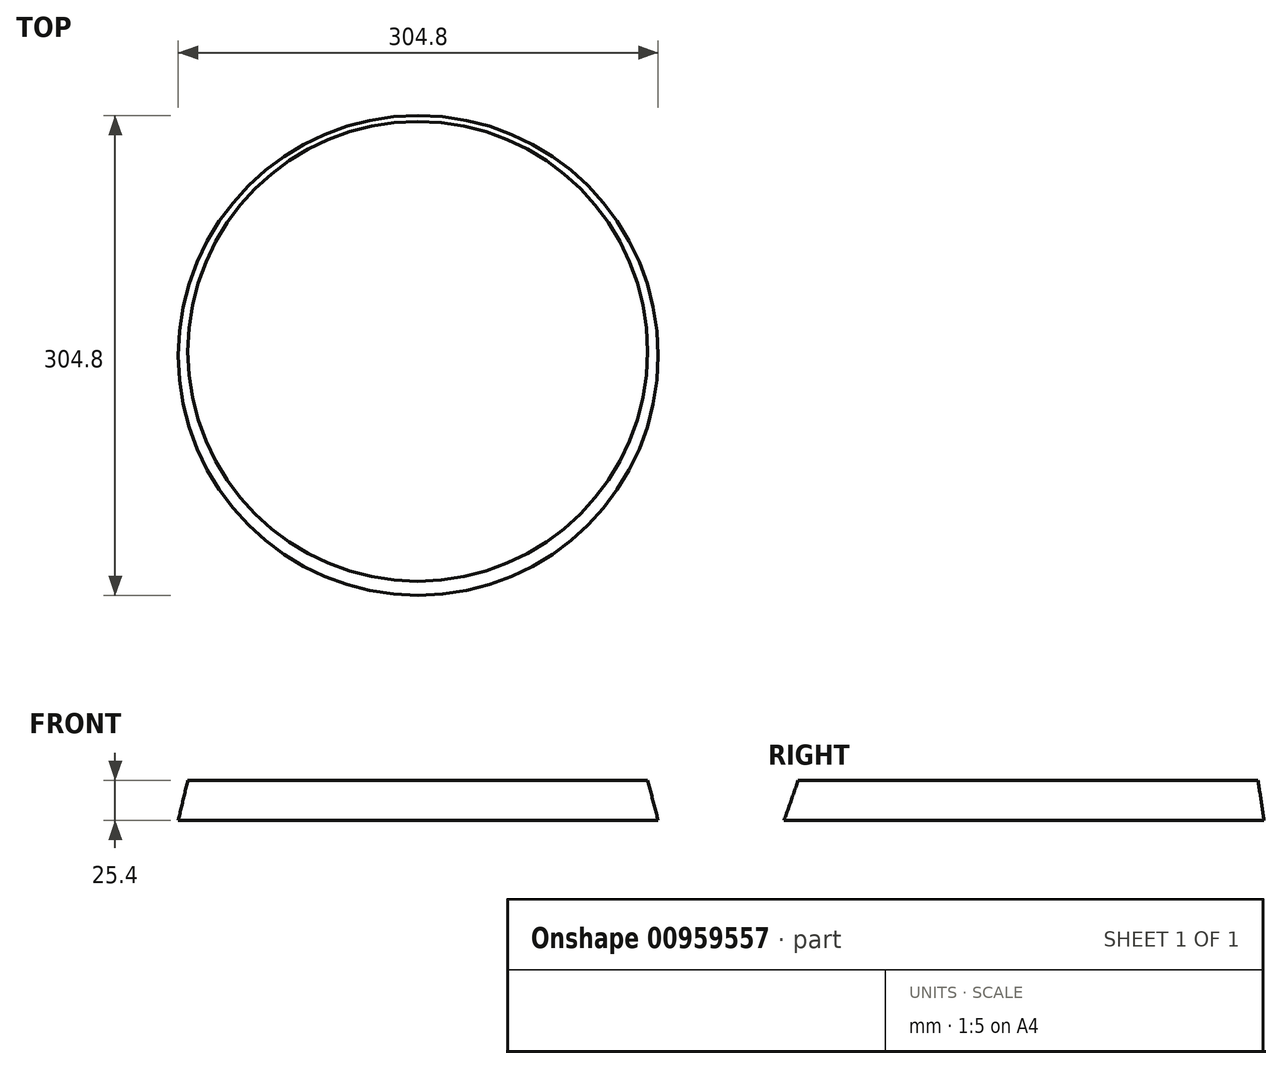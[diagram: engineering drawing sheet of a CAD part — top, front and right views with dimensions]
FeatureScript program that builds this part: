
annotation { "Feature Type Name" : "Feature", "Feature Type Description" : "" }
export const myFeature = defineFeature(function(context is Context, id is Id, definition is map)
    precondition{}
    {
        {
            var Q0;
            Q0=qCreatedBy(makeId("Top.planeOp"),FACE);
            var sketch = newSketch(context, id + "F0", { "sketchPlane" : qUnion([Q0])});
            skCircle(sketch, "E0", {"center": v(-35.68, 43.57) * mm, "radius": 152.4 * mm});
            skSolve(sketch);
        }
        {
            var Q0;
            Q0=qCreatedBy(makeId("Top.planeOp"),FACE);
            cPlane(context, id + "F1", {"entities" : qUnion([Q0]), "cplaneType" : CPlaneType.OFFSET, "offset" : 25.4 * mm, "width" : 152.4 * mm, "height" : 152.4 * mm});
        }
        {
            var Q0;
            Q0=qCreatedBy(id+"F1.planeOp",FACE);
            var sketch = newSketch(context, id + "F2", { "sketchPlane" : qUnion([Q0])});
            skCircle(sketch, "E1", {"center": v(-35.94, 46.18) * mm, "radius": 146.05 * mm});
            skSolve(sketch);
        }
        {
            var Q0;
            Q0=makeQuery(id+"F0.imprint","IMPRINT",FACE,{"disambiguationData":[TD([[makeQuery(id+"F0.imprint","IMPRINT",EDGE,{"derivedFrom":sQuery(id+"F0.wireOp",EDGE,"E0")}),1.0]])]});
            var Q1;
            Q1=makeQuery(id+"F2.imprint","IMPRINT",FACE,{"disambiguationData":[TD([[makeQuery(id+"F2.imprint","IMPRINT",EDGE,{"derivedFrom":sQuery(id+"F2.wireOp",EDGE,"E1")}),1.0]])]});
            loft(context, id + "F3", {"sheetProfilesArray" : [{ "sheetProfileEntities" : qUnion([Q0]) }, { "sheetProfileEntities" : qUnion([Q1]) }]});
        }
    });
